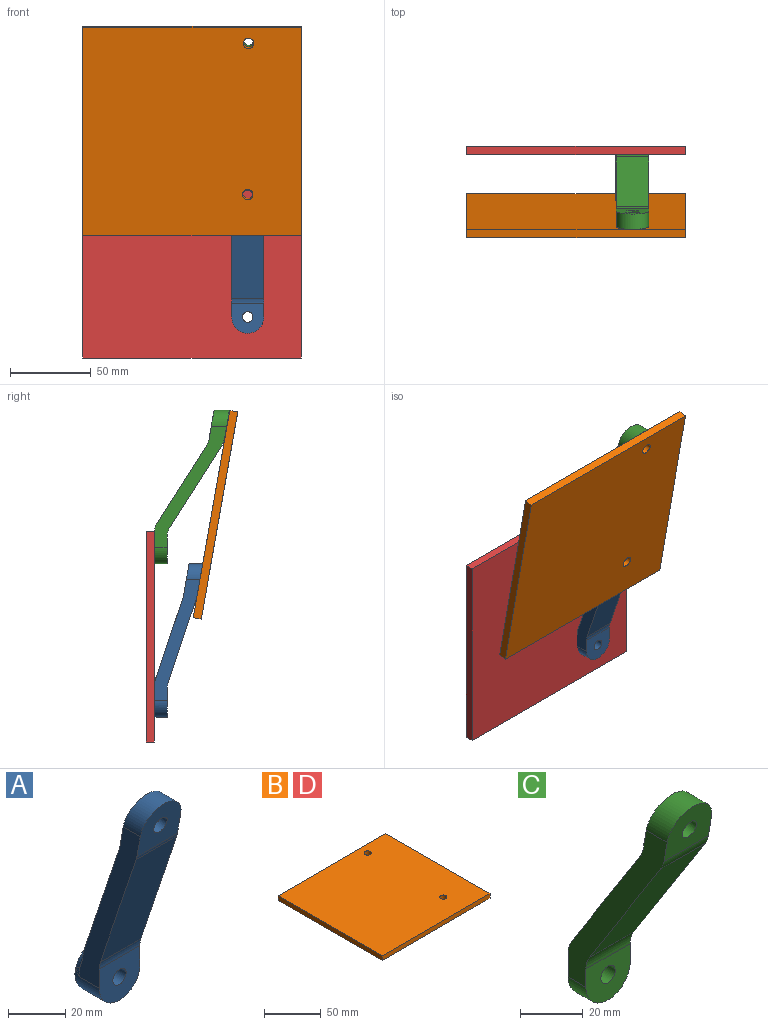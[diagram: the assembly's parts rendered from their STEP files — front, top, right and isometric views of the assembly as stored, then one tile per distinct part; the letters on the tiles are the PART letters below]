
ASSEMBLY  parts=4 mates=6
PART A: 29 faces, bbox 33.5x37.8x98.5 mm
  f0: cylinder r=3.25mm len=7.32mm, axis (0,-0.98,-0.17), area 108.5mm2, adj f6,f28
  f1: cylinder r=10mm len=20mm, axis (0,1,0), area 265.1mm2, adj f2,f5,f6,f9
  f2: plane 76.58x31.57mm, normal (-1,0,0), area 639.6mm2, adj f1,f3,f6,f7,f8,f9,f10,f12
  f3: cylinder r=10mm len=20mm, axis (0,1,0), area 384.3mm2, adj f2,f5,f7,f11,f17,f19
  f4: cylinder r=3.25mm len=12mm, axis (0,1,0), area 245mm2, adj f7,f11
  f5: plane 76.58x31.57mm, normal (1,0,0), area 639.6mm2, adj f1,f3,f6,f7,f8,f9,f10,f12
  f6: plane 23.53x22.79mm, normal (0,-0.98,-0.17), area 314.4mm2, adj f0,f1,f2,f5,f13
  f7: plane 20x18.37mm, normal (0,-1,0), area 291.2mm2, adj f2,f3,f4,f5,f12
  f8: plane 52.74x20mm, normal (0,-0.95,-0.32), area 1112.7mm2, adj f2,f5,f12,f13
  f9: plane 23.53x22.79mm, normal (0,0.98,0.17), area 285mm2, adj f1,f2,f5,f16,f22,f23,f24,f25
  f10: plane 51.44x20mm, normal (0,0.95,0.32), area 1082mm2, adj f2,f5,f14,f15,f16,f20
  f11: plane 20.1x20.1mm, normal (0,1,0), area 281mm2, adj f3,f4,f18,f20,f21
  f12: cylinder r=10mm len=20mm, axis (1,0,0), area 64.8mm2, adj f2,f5,f7,f8
  f13: cylinder r=10mm len=20mm, axis (-1,0,0), area 29.9mm2, adj f2,f5,f6,f8
  f14: cylinder r=10mm len=5.99mm, axis (-1,0,0), area 6.9mm2, adj f2,f10,f18
  f15: cylinder r=10mm len=5.99mm, axis (-1,0,0), area 6.9mm2, adj f5,f10,f21
  f16: cylinder r=10mm len=20mm, axis (1,0,0), area 29.9mm2, adj f2,f5,f9,f10
  f17: bspline ~7.5x7.45mm, area 4.4mm2, adj f2,f3,f18
  f18: bspline ~11.7x10mm, area 58.1mm2, adj f2,f11,f14,f17,f20
  f19: bspline ~7.5x7.45mm, area 4.4mm2, adj f3,f5,f21
  f20: bspline ~8.02x4.71mm, area 40.4mm2, adj f10,f11,f18,f21
  f21: bspline ~11.7x10mm, area 58.1mm2, adj f5,f11,f15,f19,f20
  f22: plane 4.25x3.38mm, normal (-0.5,-0.15,0.85), area 14.7mm2, adj f9,f23,f27,f28
  f23: plane 4.25x3.38mm, normal (0.5,-0.15,0.85), area 14.7mm2, adj f9,f22,f24,f28
  f24: plane 5.35x3.81mm, normal (1,0,0), area 14.7mm2, adj f9,f23,f25,f28
  f25: plane 4.25x3.38mm, normal (0.5,0.15,-0.85), area 14.7mm2, adj f9,f24,f26,f28
  f26: plane 4.25x3.38mm, normal (-0.5,0.15,-0.85), area 14.7mm2, adj f9,f25,f27,f28
  f27: plane 5.35x3.81mm, normal (-1,0,0), area 14.7mm2, adj f9,f22,f26,f28
  f28: plane 9.67x8.5mm, normal (0,0.98,0.17), area 29.4mm2, adj f0,f22,f23,f24,f25,f26,f27
PART B: 8 faces, bbox 135x130.1x5 mm
  f0: plane 135x5mm, normal (0,1,0), area 675mm2, adj f1,f5,f6,f7
  f1: plane 130.13x5mm, normal (-1,0,0), area 650.6mm2, adj f0,f2,f6,f7
  f2: plane 135x5mm, normal (0,-1,0), area 675mm2, adj f1,f5,f6,f7
  f3: cylinder r=3.25mm len=6.5mm, axis (0,0,-1), area 102.1mm2, adj f6,f7
  f4: cylinder r=3.25mm len=6.5mm, axis (0,0,-1), area 102.1mm2, adj f6,f7
  f5: plane 130.13x5mm, normal (1,0,0), area 650.6mm2, adj f0,f2,f6,f7
  f6: plane 135x130.13mm, normal (0,0,1), area 17500.9mm2, adj f0,f1,f2,f3,f4,f5
  f7: plane 135x130.13mm, normal (0,0,-1), area 17500.9mm2, adj f0,f1,f2,f3,f4,f5
PART C: 23 faces, bbox 20x46.5x95 mm
  f0: cylinder r=3.25mm len=7.5mm, axis (0,-0.98,-0.17), area 129.4mm2, adj f7,f22
  f1: cylinder r=10mm len=20mm, axis (0,1,0), area 297.8mm2, adj f2,f5,f7,f10
  f2: plane 75x44.73mm, normal (-1,0,0), area 694.5mm2, adj f1,f3,f6,f7,f8,f9,f10,f11
  f3: cylinder r=10mm len=20mm, axis (0,1,0), area 251.3mm2, adj f2,f5,f6,f8
  f4: cylinder r=3.25mm len=8mm, axis (0,1,0), area 163.4mm2, adj f6,f8
  f5: plane 75x44.73mm, normal (1,0,0), area 694.5mm2, adj f1,f3,f6,f7,f8,f9,f10,f11
  f6: plane 20x19.42mm, normal (0,1,0), area 312.3mm2, adj f2,f3,f4,f5,f14
  f7: plane 20x18.05mm, normal (0,-0.98,-0.17), area 289.7mm2, adj f0,f1,f2,f5,f13
  f8: plane 20x17.09mm, normal (0,-1,0), area 265.7mm2, adj f2,f3,f4,f5,f12
  f9: plane 50.87x32.34mm, normal (0,-0.84,-0.54), area 1205.6mm2, adj f2,f5,f12,f13
  f10: plane 20x18.05mm, normal (0,0.98,0.17), area 260.3mm2, adj f1,f2,f5,f15,f16,f17,f18,f19
  f11: plane 48.54x30.86mm, normal (0,0.84,0.54), area 1150.5mm2, adj f2,f5,f14,f15
  f12: cylinder r=10mm len=20mm, axis (1,0,0), area 113.3mm2, adj f2,f5,f8,f9
  f13: cylinder r=10mm len=20mm, axis (-1,0,0), area 78.4mm2, adj f2,f5,f7,f9
  f14: cylinder r=10mm len=20mm, axis (-1,0,0), area 113.3mm2, adj f2,f5,f6,f11
  f15: cylinder r=10mm len=20mm, axis (1,0,0), area 78.4mm2, adj f2,f5,f10,f11
  f16: plane 4.25x3.38mm, normal (-0.5,-0.15,0.85), area 14.7mm2, adj f10,f17,f21,f22
  f17: plane 4.25x3.38mm, normal (0.5,-0.15,0.85), area 14.7mm2, adj f10,f16,f18,f22
  f18: plane 5.35x3.81mm, normal (1,0,0), area 14.7mm2, adj f10,f17,f19,f22
  f19: plane 4.25x3.38mm, normal (0.5,0.15,-0.85), area 14.7mm2, adj f10,f18,f20,f22
  f20: plane 4.25x3.38mm, normal (-0.5,0.15,-0.85), area 14.7mm2, adj f10,f19,f21,f22
  f21: plane 5.35x3.81mm, normal (-1,0,0), area 14.7mm2, adj f10,f16,f20,f22
  f22: plane 9.67x8.5mm, normal (0,0.98,0.17), area 29.4mm2, adj f0,f16,f17,f18,f19,f20,f21
PART D: same geometry as B
PLACE A t=(108,-8.21,-146.76)mm
PLACE B rot(axis=(1,0,0),100deg) t=(94.66,-51.22,-21.18)mm
PLACE C t=(108.54,-8.21,-51.76)mm
PLACE D rot(axis=(1,0,0),90deg) t=(94.66,-3.21,-96.47)mm
MATE planar A.f6 <-> B.f7  axis (0,-0.98,-0.17) through (118,-36.45,-104.98)mm
MATE planar C.f6 <-> D.f6  axis (0,1,0) through (108.54,-8.21,-84.28)mm
MATE cylindrical A.f3 <-> D.f3  axis (0,-1,0) through (108,-16.21,-179.98)mm
MATE parallel C.f5 <-> D.f5  axis (1,0,0) through (118.54,-25.2,-45.93)mm
MATE cylindrical C.f3 <-> D.f4  axis (0,1,0) through (108.54,-12.21,-84.98)mm
MATE parallel A.f5 <-> D.f5  axis (1,0,0) through (118,-21.2,-142.85)mm
